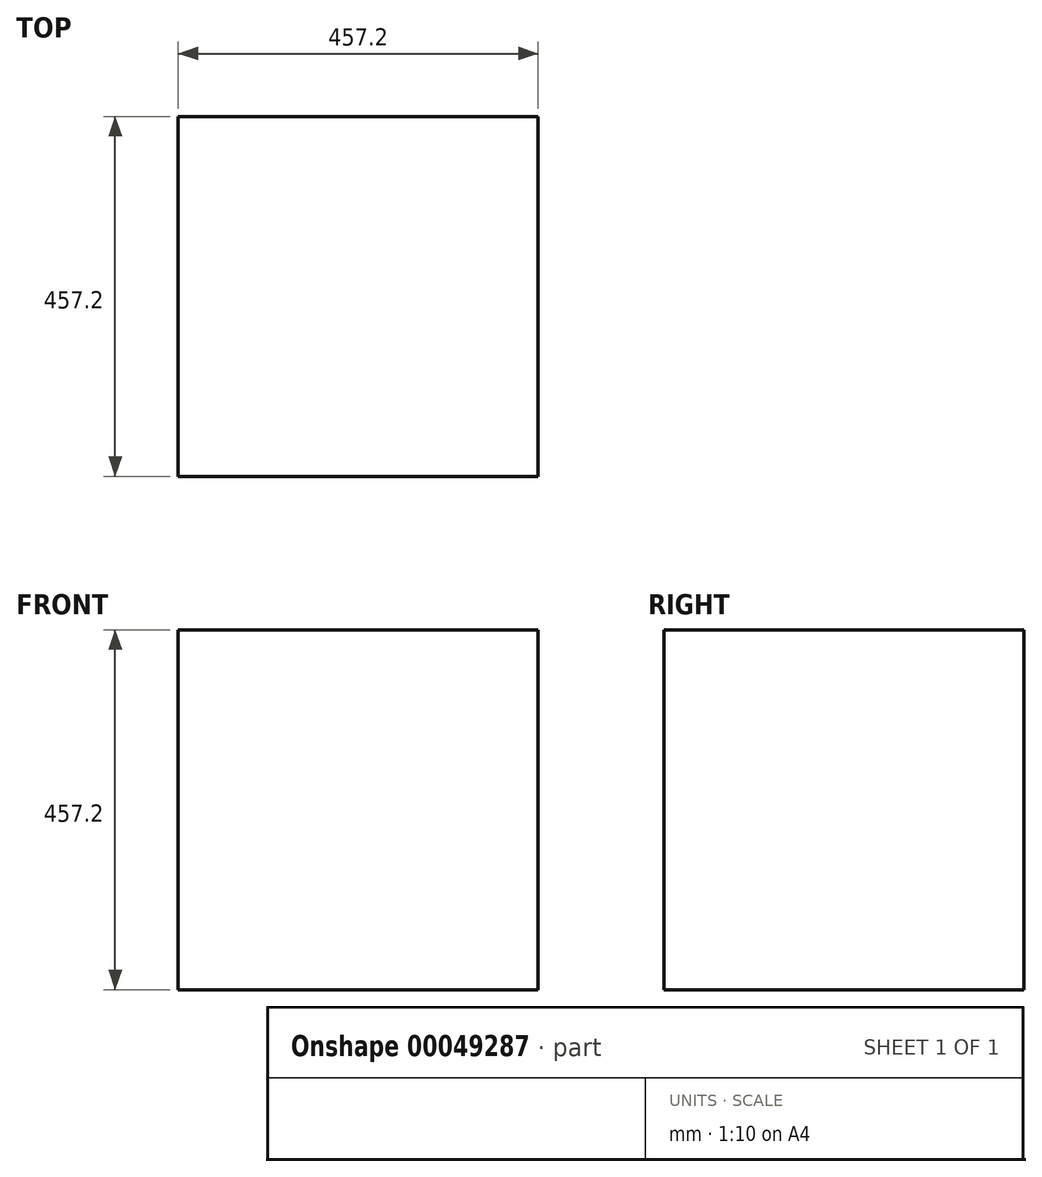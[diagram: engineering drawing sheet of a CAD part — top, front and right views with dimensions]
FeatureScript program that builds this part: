
annotation { "Feature Type Name" : "Feature", "Feature Type Description" : "" }
export const myFeature = defineFeature(function(context is Context, id is Id, definition is map)
    precondition{}
    {
        {
            var Q0;
            Q0=qCreatedBy(makeId("Top.planeOp"),FACE);
            var sketch = newSketch(context, id + "F0", { "sketchPlane" : qUnion([Q0])});
            skLineSegment(sketch, "E0.rect.bottom", {"start": v(228.6, 229.13) * mm, "end": v(-228.6, 229.13) * mm});
            skLineSegment(sketch, "E0.rect.top", {"start": v(228.6, -228.07) * mm, "end": v(-228.6, -228.07) * mm});
            skLineSegment(sketch, "E0.rect.left", {"start": v(228.6, 229.13) * mm, "end": v(228.6, -228.07) * mm});
            skLineSegment(sketch, "E0.rect.right", {"start": v(-228.6, 229.13) * mm, "end": v(-228.6, -228.07) * mm});
            skPoint(sketch, "E0.rect.middle", {"position": v(0, 0.53) * mm});
            skSolve(sketch);
        }
        {
            var Q0;
            Q0 = qSketchRegion(id + "F0", true);
            extrude(context, id + "F1", {"entities" : qUnion([Q0]), "depth" : 457.2 * mm});
        }
    });
